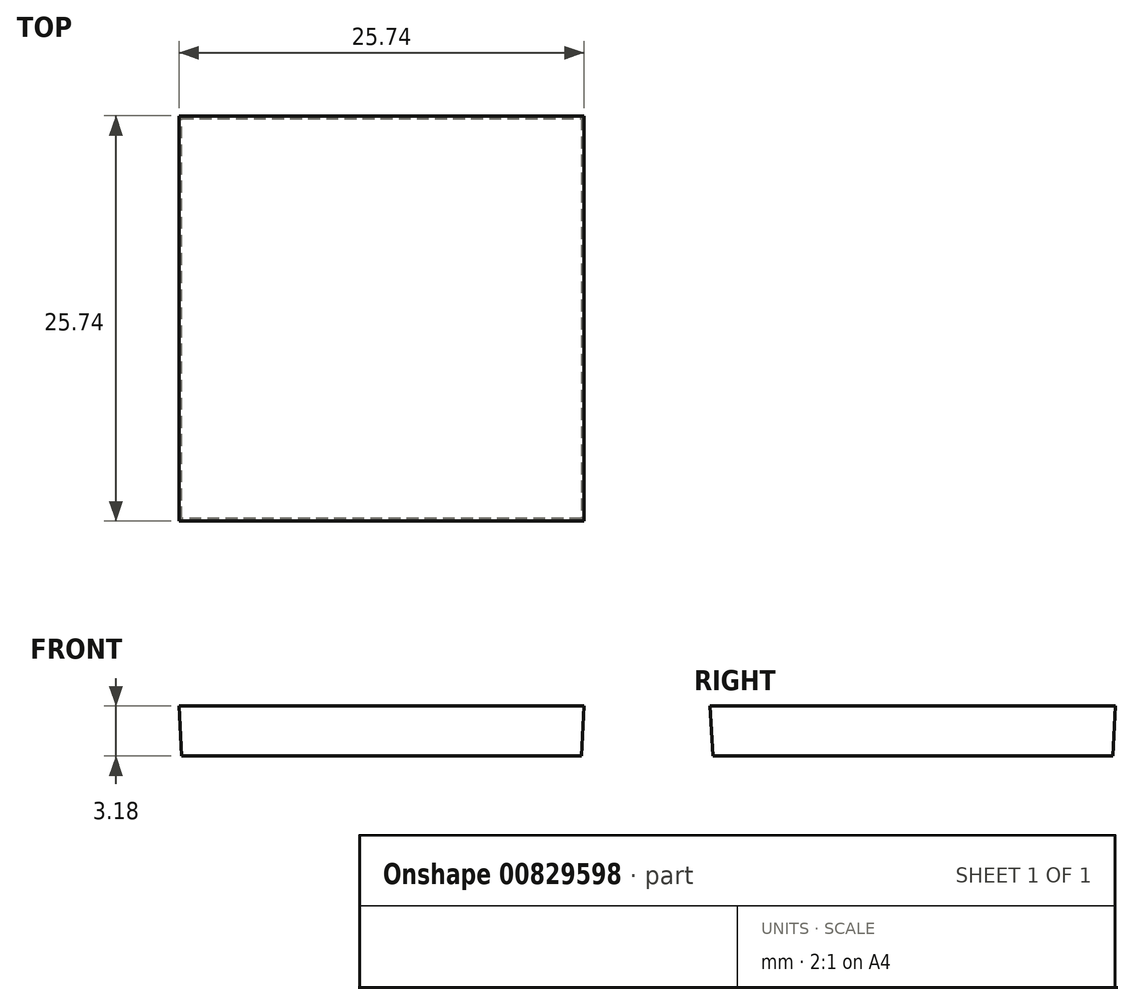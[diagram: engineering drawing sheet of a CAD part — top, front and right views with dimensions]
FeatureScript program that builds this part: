
annotation { "Feature Type Name" : "Feature", "Feature Type Description" : "" }
export const myFeature = defineFeature(function(context is Context, id is Id, definition is map)
    precondition{}
    {
        {
            var Q0;
            Q0=qCreatedBy(makeId("Top.planeOp"),FACE);
            var sketch = newSketch(context, id + "F0", { "sketchPlane" : qUnion([Q0])});
            skLineSegment(sketch, "E0.bottom", {"start": v(12.7, 12.7) * mm, "end": v(-12.7, 12.7) * mm});
            skLineSegment(sketch, "E0.top", {"start": v(12.7, -12.7) * mm, "end": v(-12.7, -12.7) * mm});
            skLineSegment(sketch, "E0.left", {"start": v(12.7, 12.7) * mm, "end": v(12.7, -12.7) * mm});
            skLineSegment(sketch, "E0.right", {"start": v(-12.7, 12.7) * mm, "end": v(-12.7, -12.7) * mm});
            skPoint(sketch, "E0.middle", {"position": v(0, 0) * mm});
            skSolve(sketch);
        }
        {
            var Q0;
            Q0 = qSketchRegion(id + "F0", true);
            extrude(context, id + "F1", {"entities" : qUnion([Q0]), "depth" : 3.17 * mm, "offsetDistance" : 25 * mm, "hasDraft" : true, "draftAngle" : 3 * degree});
        }
    });
